# Revit family: SIB_Precast-Beam with Slope_Spæncom
name_source: partatom
category: Structural Framing
revit_build: Autodesk Revit 2014 (Build: 20130308_1515(x64)
units: mm (PartAtom-declared; Revit-internal decimal feet)

## types (21) — shared parameters
Manufacturer = Spæncom
Mirror base RB = 80 mm  [stored 0.262467 ft]

## per-type parameters (varying)
| type | Height KIP | Mirror Depth end | Mirror base IB | Mirror thickness | Mirror top IB | Mirror top RB | Model | Width Element |
| SIB 24/108 | 1080 mm  [stored 3.54331 ft] | 100 mm  [stored 0.328084 ft] | 80 mm  [stored 0.262467 ft] | 80 mm  [stored 0.262467 ft] | 80 mm  [stored 0.262467 ft] | 100 mm  [stored 0.328084 ft] | SIB 24/108 | 240 mm  [stored 0.787402 ft] |
| SIB24/72 | 720 mm  [stored 2.3622 ft] | 80 mm  [stored 0.262467 ft] | 80 mm  [stored 0.262467 ft] | 80 mm  [stored 0.262467 ft] | 80 mm  [stored 0.262467 ft] | 100 mm  [stored 0.328084 ft] | SIB 24/72 | 240 mm  [stored 0.787402 ft] |
| SIB24/84 | 840 mm  [stored 2.75591 ft] | 80 mm  [stored 0.262467 ft] | 80 mm  [stored 0.262467 ft] | 80 mm  [stored 0.262467 ft] | 80 mm  [stored 0.262467 ft] | 100 mm  [stored 0.328084 ft] | SIB 24/84 | 240 mm  [stored 0.787402 ft] |
| SIB24/96 | 960 mm  [stored 3.14961 ft] | 80 mm  [stored 0.262467 ft] | 80 mm  [stored 0.262467 ft] | 80 mm  [stored 0.262467 ft] | 80 mm  [stored 0.262467 ft] | 100 mm  [stored 0.328084 ft] | SIB24/96 | 240 mm  [stored 0.787402 ft] |
| SIB30/108 | 1080 mm  [stored 3.54331 ft] | 110 mm  [stored 0.360892 ft] | 110 mm  [stored 0.360892 ft] | 80 mm  [stored 0.262467 ft] | 80 mm  [stored 0.262467 ft] | 140 mm  [stored 0.459318 ft] | SIB 30/108 | 300 mm |
| SIB30/120 | 1200 mm | 110 mm  [stored 0.360892 ft] | 110 mm  [stored 0.360892 ft] | 80 mm  [stored 0.262467 ft] | 80 mm  [stored 0.262467 ft] | 140 mm  [stored 0.459318 ft] | SIB 30/120 | 300 mm |
| SIB30/132 | 1320 mm | 110 mm  [stored 0.360892 ft] | 110 mm  [stored 0.360892 ft] | 80 mm  [stored 0.262467 ft] | 80 mm  [stored 0.262467 ft] | 140 mm  [stored 0.459318 ft] | SIB 30/132 | 300 mm |
| SIB30/144 | 1440 mm  [stored 4.72441 ft] | 110 mm  [stored 0.360892 ft] | 110 mm  [stored 0.360892 ft] | 80 mm  [stored 0.262467 ft] | 80 mm  [stored 0.262467 ft] | 140 mm  [stored 0.459318 ft] | SIB 30/144 | 300 mm |
| SIB36/108 | 1080 mm  [stored 3.54331 ft] | 110 mm  [stored 0.360892 ft] | 110 mm  [stored 0.360892 ft] | 140 mm  [stored 0.459318 ft] | 80 mm  [stored 0.262467 ft] | 140 mm  [stored 0.459318 ft] | SIB 36/108 | 360 mm  [stored 1.1811 ft] |
| SIB36/120 | 1200 mm | 110 mm  [stored 0.360892 ft] | 110 mm  [stored 0.360892 ft] | 140 mm  [stored 0.459318 ft] | 80 mm  [stored 0.262467 ft] | 140 mm  [stored 0.459318 ft] | SIB 36/120 | 360 mm  [stored 1.1811 ft] |
| SIB36/132 | 1320 mm | 110 mm  [stored 0.360892 ft] | 110 mm  [stored 0.360892 ft] | 140 mm  [stored 0.459318 ft] | 80 mm  [stored 0.262467 ft] | 140 mm  [stored 0.459318 ft] | SIB 36/132 | 360 mm  [stored 1.1811 ft] |
| SIB36/144 | 1440 mm  [stored 4.72441 ft] | 110 mm  [stored 0.360892 ft] | 110 mm  [stored 0.360892 ft] | 140 mm  [stored 0.459318 ft] | 80 mm  [stored 0.262467 ft] | 140 mm  [stored 0.459318 ft] | SIB 36/144 | 360 mm  [stored 1.1811 ft] |
| SIB36/156 | 1560 mm  [stored 5.11811 ft] | 110 mm  [stored 0.360892 ft] | 110 mm  [stored 0.360892 ft] | 140 mm  [stored 0.459318 ft] | 80 mm  [stored 0.262467 ft] | 140 mm  [stored 0.459318 ft] | SIB 36/156 | 360 mm  [stored 1.1811 ft] |
| SIB42/144 | 1440 mm  [stored 4.72441 ft] | 110 mm  [stored 0.360892 ft] | 170 mm  [stored 0.557743 ft] | 80 mm  [stored 0.262467 ft] | 100 mm  [stored 0.328084 ft] | 120 mm  [stored 0.393701 ft] | SIB 42/144 | 420 mm  [stored 1.37795 ft] |
| SIB42/156 | 1560 mm  [stored 5.11811 ft] | 110 mm  [stored 0.360892 ft] | 170 mm  [stored 0.557743 ft] | 80 mm  [stored 0.262467 ft] | 100 mm  [stored 0.328084 ft] | 120 mm  [stored 0.393701 ft] | SIB 42/156 | 420 mm  [stored 1.37795 ft] |
| SIB42/168 | 1680 mm  [stored 5.51181 ft] | 110 mm  [stored 0.360892 ft] | 170 mm  [stored 0.557743 ft] | 80 mm  [stored 0.262467 ft] | 100 mm  [stored 0.328084 ft] | 120 mm  [stored 0.393701 ft] | SIB 42/168 | 420 mm  [stored 1.37795 ft] |
| SIB42/180 | 1800 mm  [stored 5.90551 ft] | 110 mm  [stored 0.360892 ft] | 170 mm  [stored 0.557743 ft] | 80 mm  [stored 0.262467 ft] | 100 mm  [stored 0.328084 ft] | 120 mm  [stored 0.393701 ft] | SIB 42/180 | 420 mm  [stored 1.37795 ft] |
| SIB42/192 | 1920 mm  [stored 6.29921 ft] | 110 mm  [stored 0.360892 ft] | 170 mm  [stored 0.557743 ft] | 80 mm  [stored 0.262467 ft] | 100 mm  [stored 0.328084 ft] | 120 mm  [stored 0.393701 ft] | SIB 42/192 | 420 mm  [stored 1.37795 ft] |
| SIB42/204 | 2040 mm  [stored 6.69291 ft] | 110 mm  [stored 0.360892 ft] | 170 mm  [stored 0.557743 ft] | 80 mm  [stored 0.262467 ft] | 100 mm  [stored 0.328084 ft] | 120 mm  [stored 0.393701 ft] | SIB 42/204 | 420 mm  [stored 1.37795 ft] |
| SIB42/216 | 2160 mm  [stored 7.08661 ft] | 110 mm  [stored 0.360892 ft] | 170 mm  [stored 0.557743 ft] | 80 mm  [stored 0.262467 ft] | 100 mm  [stored 0.328084 ft] | 120 mm  [stored 0.393701 ft] | SIB 42/216 | 420 mm  [stored 1.37795 ft] |
| SIB42/228 | 2280 mm  [stored 7.48031 ft] | 110 mm  [stored 0.360892 ft] | 170 mm  [stored 0.557743 ft] | 80 mm  [stored 0.262467 ft] | 100 mm  [stored 0.328084 ft] | 120 mm  [stored 0.393701 ft] | SIB 42/228 | 420 mm  [stored 1.37795 ft] |

note: [stored X ft] marks values corroborated as IEEE doubles in the binary element streams (Revit-internal decimal feet)

## geometry (parser evidence)
native form markers: Sweep x1
no freeform markers — native parametric forms only
